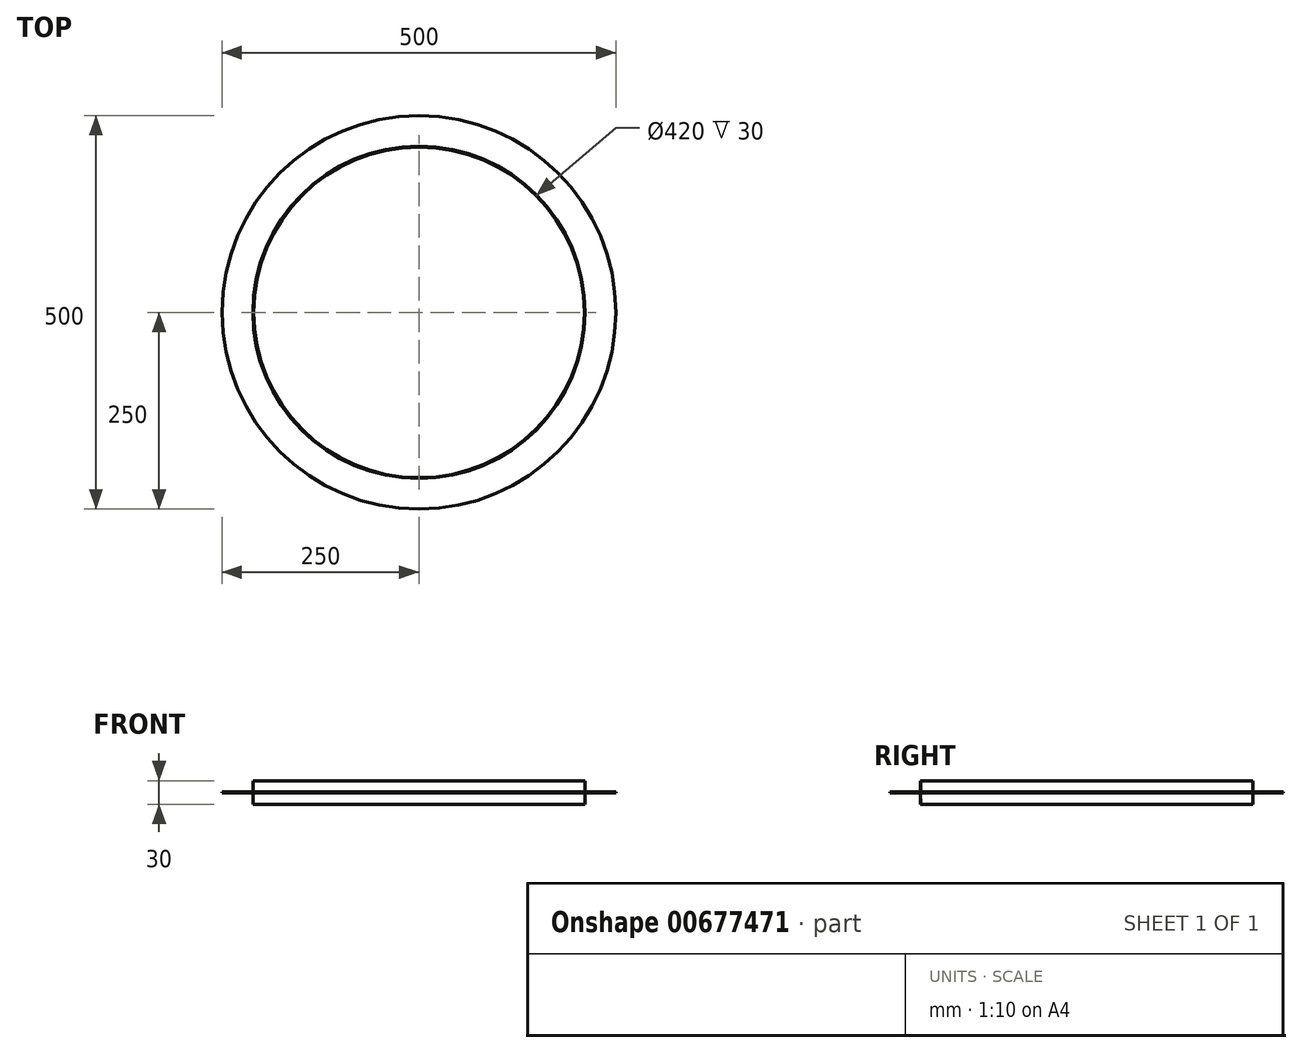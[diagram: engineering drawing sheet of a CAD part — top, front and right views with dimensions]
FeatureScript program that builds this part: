
annotation { "Feature Type Name" : "Feature", "Feature Type Description" : "" }
export const myFeature = defineFeature(function(context is Context, id is Id, definition is map)
    precondition{}
    {
        {
            var Q0;
            Q0=qCreatedBy(makeId("Top.planeOp"),FACE);
            var sketch = newSketch(context, id + "F0", { "sketchPlane" : qUnion([Q0])});
            skCircle(sketch, "E0", {"center": v(0, 0) * mm, "radius": 210 * mm});
            skCircle(sketch, "E1", {"center": v(0, 0) * mm, "radius": 250 * mm});
            skCircle(sketch, "E2", {"center": v(0, 0) * mm, "radius": 200 * mm});
            skCircle(sketch, "E3", {"center": v(0, 0) * mm, "radius": 211 * mm});
            skCircle(sketch, "E4", {"center": v(0, 0) * mm, "radius": 190 * mm});
            skSolve(sketch);
        }
        {
            var Q0;
            Q0=makeQuery(id+"F0.imprint","IMPRINT",FACE,{"disambiguationData":[TD([[makeQuery(id+"F0.imprint","IMPRINT",EDGE,{"derivedFrom":sQuery(id+"F0.wireOp",EDGE,"E0")}),-1.0]])]});
            extrude(context, id + "F1", {"entities" : qUnion([Q0]), "depth" : 15 * mm, "offsetDistance" : 25 * mm, "hasSecondDirection" : true, "secondDirectionOppositeDirection" : true, "secondDirectionDepth" : 15 * mm});
        }
        {
            var Q0;
            Q0 = qSketchRegion(id + "F0", true);
            extrude(context, id + "F2", {"entities" : qUnion([Q0]), "operationType" : NewBodyOperationType.ADD, "depth" : 0.5 * mm, "offsetDistance" : 25 * mm, "hasSecondDirection" : true, "secondDirectionOppositeDirection" : true, "secondDirectionDepth" : 0.5 * mm});
        }
    });
